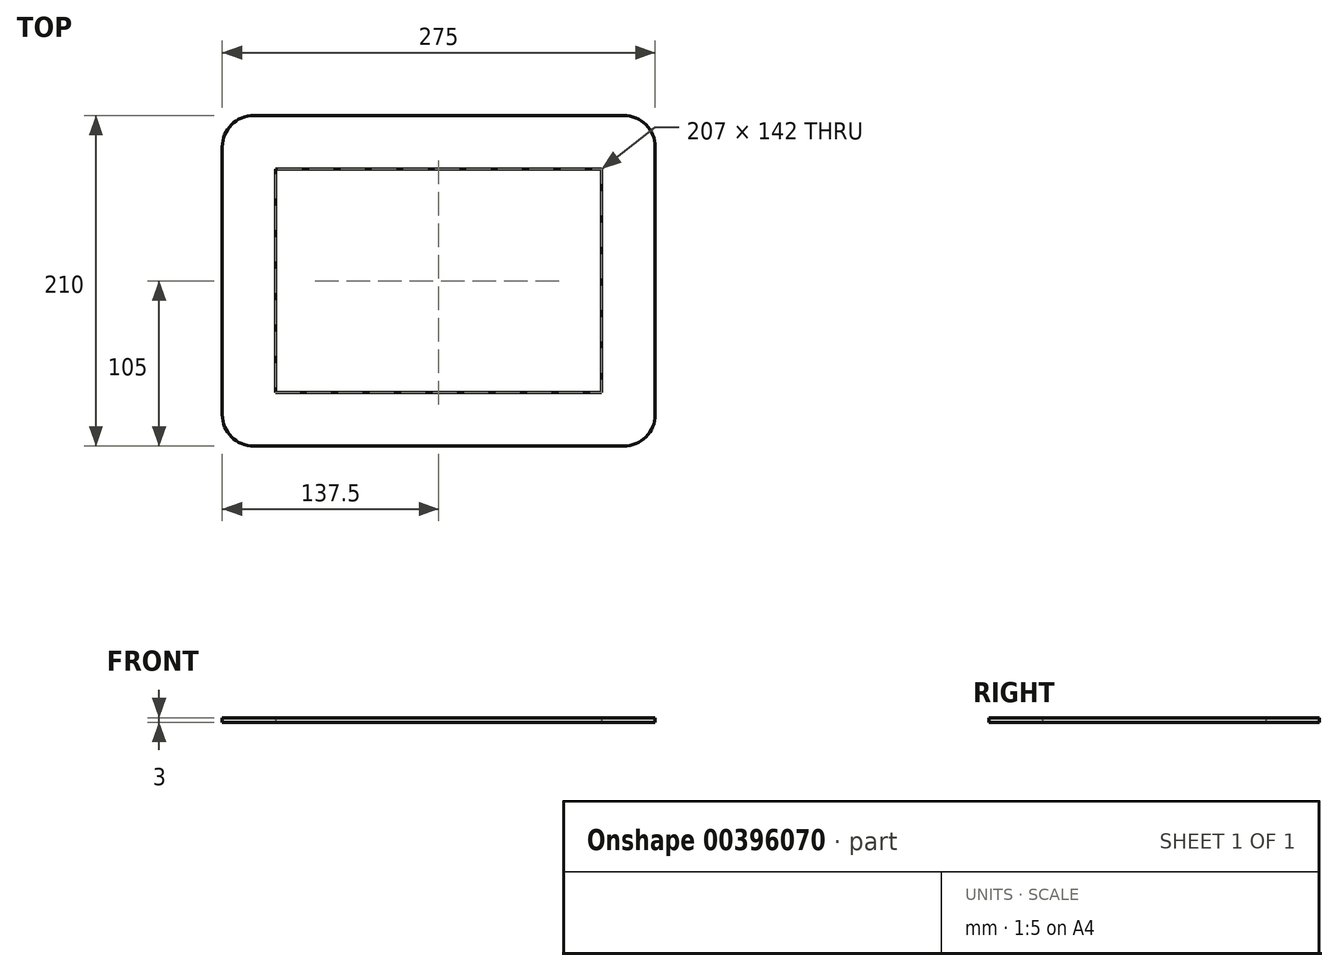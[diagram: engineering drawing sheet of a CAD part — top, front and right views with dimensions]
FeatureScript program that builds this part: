
annotation { "Feature Type Name" : "Feature", "Feature Type Description" : "" }
export const myFeature = defineFeature(function(context is Context, id is Id, definition is map)
    precondition{}
    {
        {
            var Q0;
            Q0=qCreatedBy(makeId("Top.planeOp"),FACE);
            var sketch = newSketch(context, id + "F0", { "sketchPlane" : qUnion([Q0])});
            skLineSegment(sketch, "E0.bottom", {"start": v(-117.5, 105) * mm, "end": v(117.5, 105) * mm});
            skLineSegment(sketch, "E0.top", {"start": v(-117.5, -105) * mm, "end": v(117.5, -105) * mm});
            skLineSegment(sketch, "E0.left", {"start": v(-137.5, 85) * mm, "end": v(-137.5, -85) * mm});
            skLineSegment(sketch, "E0.right", {"start": v(137.5, 85) * mm, "end": v(137.5, -85) * mm});
            skPoint(sketch, "E0.middle", {"position": v(0, 0) * mm});
            skPoint(sketch, "E1.visualSharp", {"position": v(-137.5, 105) * mm});
            skArc(sketch, "E1.filletArc", {"start": v(-117.5, 105) * mm, "mid": v(-131.64, 99.14) * mm, "end": v(-137.5, 85) * mm});
            skPoint(sketch, "E2.visualSharp", {"position": v(-137.5, -105) * mm});
            skArc(sketch, "E2.filletArc", {"start": v(-137.5, -85) * mm, "mid": v(-131.64, -99.14) * mm, "end": v(-117.5, -105) * mm});
            skPoint(sketch, "E3.visualSharp", {"position": v(137.5, -105) * mm});
            skArc(sketch, "E3.filletArc", {"start": v(117.5, -105) * mm, "mid": v(131.64, -99.14) * mm, "end": v(137.5, -85) * mm});
            skPoint(sketch, "E4.visualSharp", {"position": v(137.5, 105) * mm});
            skArc(sketch, "E4.filletArc", {"start": v(137.5, 85) * mm, "mid": v(131.64, 99.14) * mm, "end": v(117.5, 105) * mm});
            skLineSegment(sketch, "E5.bottom", {"start": v(-103.5, 71) * mm, "end": v(103.5, 71) * mm});
            skLineSegment(sketch, "E5.top", {"start": v(-103.5, -71) * mm, "end": v(103.5, -71) * mm});
            skLineSegment(sketch, "E5.left", {"start": v(-103.5, 71) * mm, "end": v(-103.5, -71) * mm});
            skLineSegment(sketch, "E5.right", {"start": v(103.5, 71) * mm, "end": v(103.5, -71) * mm});
            skSolve(sketch);
        }
        {
            var Q0;
            Q0=qSketchRegion(id+"F0",true);
            extrude(context, id + "F1", {"entities" : qUnion([Q0]), "depth" : 3 * mm});
        }
    });
